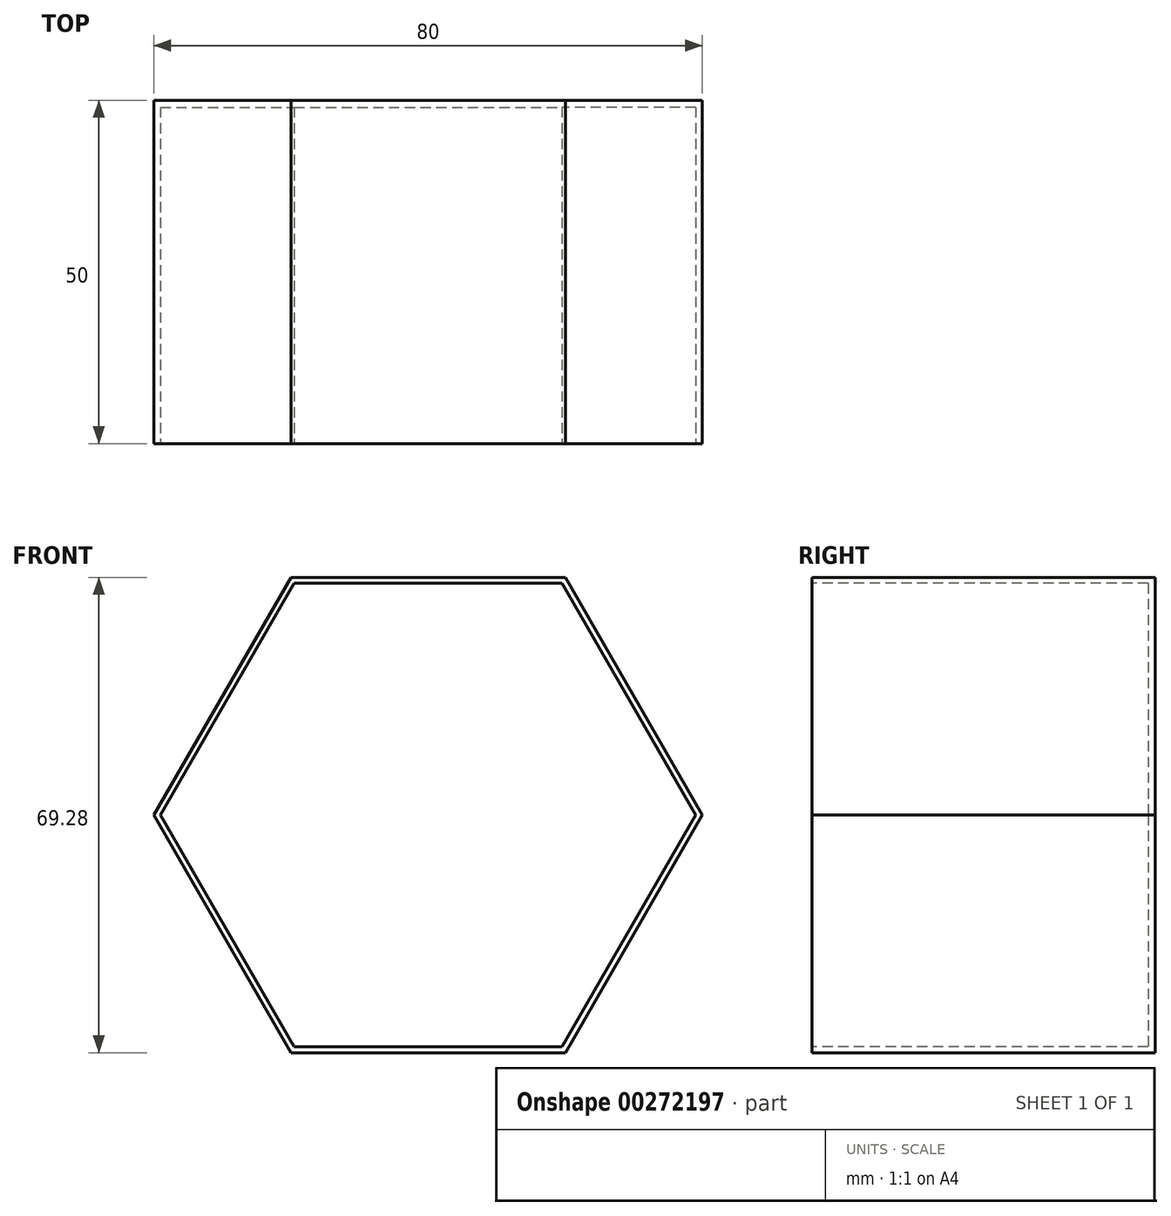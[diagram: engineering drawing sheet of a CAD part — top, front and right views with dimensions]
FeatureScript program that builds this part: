
annotation { "Feature Type Name" : "Feature", "Feature Type Description" : "" }
export const myFeature = defineFeature(function(context is Context, id is Id, definition is map)
    precondition{}
    {
        {
            var Q0;
            Q0=qCreatedBy(makeId("Front.planeOp"),FACE);
            var sketch = newSketch(context, id + "F0", { "sketchPlane" : qUnion([Q0])});
            skCircle(sketch, "E0.cCircle", {"center": v(0, 0) * mm, "radius": 34.64 * mm, "construction": true});
            skLineSegment(sketch, "E0.0", {"start": v(20, 34.64) * mm, "end": v(40, 0) * mm});
            skLineSegment(sketch, "E0.1", {"start": v(40, 0) * mm, "end": v(20, -34.64) * mm});
            skLineSegment(sketch, "E0.2", {"start": v(20, -34.64) * mm, "end": v(-20, -34.64) * mm});
            skLineSegment(sketch, "E0.3", {"start": v(-20, -34.64) * mm, "end": v(-40, 0) * mm});
            skLineSegment(sketch, "E0.4", {"start": v(-40, 0) * mm, "end": v(-20, 34.64) * mm});
            skLineSegment(sketch, "E0.5", {"start": v(-20, 34.64) * mm, "end": v(20, 34.64) * mm});
            skPoint(sketch, "E0.0.midPoint", {"position": v(30, 17.32) * mm});
            skSolve(sketch);
        }
        {
            var Q0;
            Q0=makeQuery(id+"F0.imprint","IMPRINT",FACE,{"disambiguationData":[TD([[makeQuery(id+"F0.imprint","IMPRINT",EDGE,{"derivedFrom":sQuery(id+"F0.wireOp",EDGE,"E0.0")}),-1.0]])]});
            extrude(context, id + "F1", {"entities" : qUnion([Q0]), "depth" : 50 * mm});
        }
        {
            var Q0;
            Q0=makeQuery(id+"F1.opExtrude","CAP_FACE",FACE,{"disambiguationData":[OSD([sQuery(id+"F0.wireOp",EDGE,"E0.0"),sQuery(id+"F0.wireOp",EDGE,"E0.1"),sQuery(id+"F0.wireOp",EDGE,"E0.2"),sQuery(id+"F0.wireOp",EDGE,"E0.3"),sQuery(id+"F0.wireOp",EDGE,"E0.4"),sQuery(id+"F0.wireOp",EDGE,"E0.5")])],"isStart":false});
            var sketch = newSketch(context, id + "F2", { "sketchPlane" : qUnion([Q0])});
            skCircle(sketch, "E1.cCircle", {"center": v(0, 0) * mm, "radius": 33.77 * mm, "construction": true});
            skLineSegment(sketch, "E1.0", {"start": v(39, 0) * mm, "end": v(19.5, -33.77) * mm});
            skLineSegment(sketch, "E1.1", {"start": v(19.5, -33.77) * mm, "end": v(-19.5, -33.77) * mm});
            skLineSegment(sketch, "E1.2", {"start": v(-19.5, -33.77) * mm, "end": v(-39, 0) * mm});
            skLineSegment(sketch, "E1.3", {"start": v(-39, 0) * mm, "end": v(-19.5, 33.77) * mm});
            skLineSegment(sketch, "E1.4", {"start": v(-19.5, 33.77) * mm, "end": v(19.5, 33.77) * mm});
            skLineSegment(sketch, "E1.5", {"start": v(19.5, 33.77) * mm, "end": v(39, 0) * mm});
            skPoint(sketch, "E1.0.midPoint", {"position": v(29.25, -16.89) * mm});
            skSolve(sketch);
        }
        {
            var Q0;
            Q0=makeQuery(id+"F2.imprint","IMPRINT",FACE,{"disambiguationData":[TD([[makeQuery(id+"F2.imprint","IMPRINT",EDGE,{"derivedFrom":sQuery(id+"F2.wireOp",EDGE,"E1.0")}),-1.0]])]});
            extrude(context, id + "F3", {"entities" : qUnion([Q0]), "operationType" : NewBodyOperationType.REMOVE, "oppositeDirection" : true, "depth" : 49 * mm});
        }
    });
